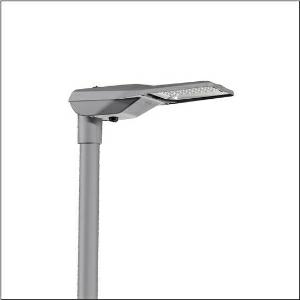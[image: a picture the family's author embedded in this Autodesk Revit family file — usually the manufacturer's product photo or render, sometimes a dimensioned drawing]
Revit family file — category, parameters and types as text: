
# Revit family: streetlight_sl_21_mini___st1_0a_5xe2d63t08hb_d890
name_source: partatom
category: Lighting Fixtures
units: mm (PartAtom-declared; Revit-internal decimal feet)

## family parameters
Cut with Voids When Loaded = No
Host = Face
Light Source = No
Part Type = Normal
Room Calculation Point = No
Round Connector Dimension = Use Diameter
Shared = No

## types (1)
- --- (1 x LED, 8110 lm, 66 W, 2700K)
    Apparent Load = 66 VA
    CIE Flux Codes = 37 72 97 100 100
    Color Rendering = 70
    Color Temperature = 2700K
    Default Elevation = 1800 mm
    Description = Streetlight SL 21 mini, mast luminaire, primary light control with lens, of PMMA, primary optical cover: cover, of toughened safety glass, transparent, light distribution: ST1.0a, light emission: direct distribution, primary light characteristic: asymmetric, installation type: side-entry, post-top, LED, High Power LED, rated luminous flux: 8.110lm, luminous efficacy: 123lm/W, light colour: 727, colour temperature: 2700K, control gear: D4i, control: overheat protection, constant luminous flux control, time-dependent luminous flux control, flexible luminous flux parameterisation, pre-setting: logarithmic dimming characteristic, mains connection: 220..240V, AC, 50/60Hz, start of lifetime: 66W, end of service life: 69W, reduction: 30W, luminaire housing, of diecast aluminium, powder-coated, SITECO metallic grey (DB 702S), corrosivity category C5 high according to DIN EN ISO 12944, please order mast flange separately, inclination adjustable: 0°, 5°, 10°, 15°, sealing non-destructively replaceable, multi-level sealing system, length: 628mm, width: 235mm, height: 110mm, mast flange for spigot size: 42mm (side-entry): 5XC10008XM4, 60/48mm (side-entry/post-top): 5XC10108XM2, 76/60mm (side-entry/post-top): 5XC10108XM1, mounting height: 4..8m, Smart Interface below and above, protection rating (complete): IP66, insulation class (complete): insulation class II (safety insulation), certification: CE, ENEC, ENEC+, VDE, impact resistance: IK10, permissible operating ambient temperature for outdoor applications: -40..+50°C, standard-compliant lighting for roads and squares, packaging unit: 1 piece

Light Distribution: ST1.0a
    Height = 110 mm
    Lamp = 1 x LED
    Lamp Light Flux = 8110 lm
    Lamp Power = 66 W
    Lamp count = 1
    Length = 625 mm
    Luminous efficacy = 123 lm/W
    Manufacturer = Siteco
    ModVariant = No
    Model = 5XE2D63T08HB
    Number of Poles = 1
    OnlyDefault = Yes
    Power Factor = 1
    Product Name = Streetlight SL 21 mini | ST1.0a
    Product group = mast luminaire | pylon top
    ProductGroupID = 6100
    Protection Class = Protection class II
    Protection Degree = IP 66
    RLX_Detail_Level = 1
    RLX_Emergency_Light_Flux = 0 lm
    RLX_Emergency_Type = 0
    RLX_Emergency_Type_DB = No
    RlxData = <blob elided: 26221 chars, md5=033ec4e2>
    Socket = socket
    Standby Power = 0 W
    System Light Flux = 8110 lm
    System Power = 66 W
    Type Comments = factory setting: luminous flux: 100 % | dim-lin: 254 | 670 mA
    Type Image = l_1003514.jpg
    URL = http://relux.com
    VarID = @adj_185863
    Voltage = 0 V
    Weight = 0.00 kg
    Width = 234 mm

## geometry (parser evidence)
native form markers: Blend x4, Sweep x10
no freeform markers — native parametric forms only
